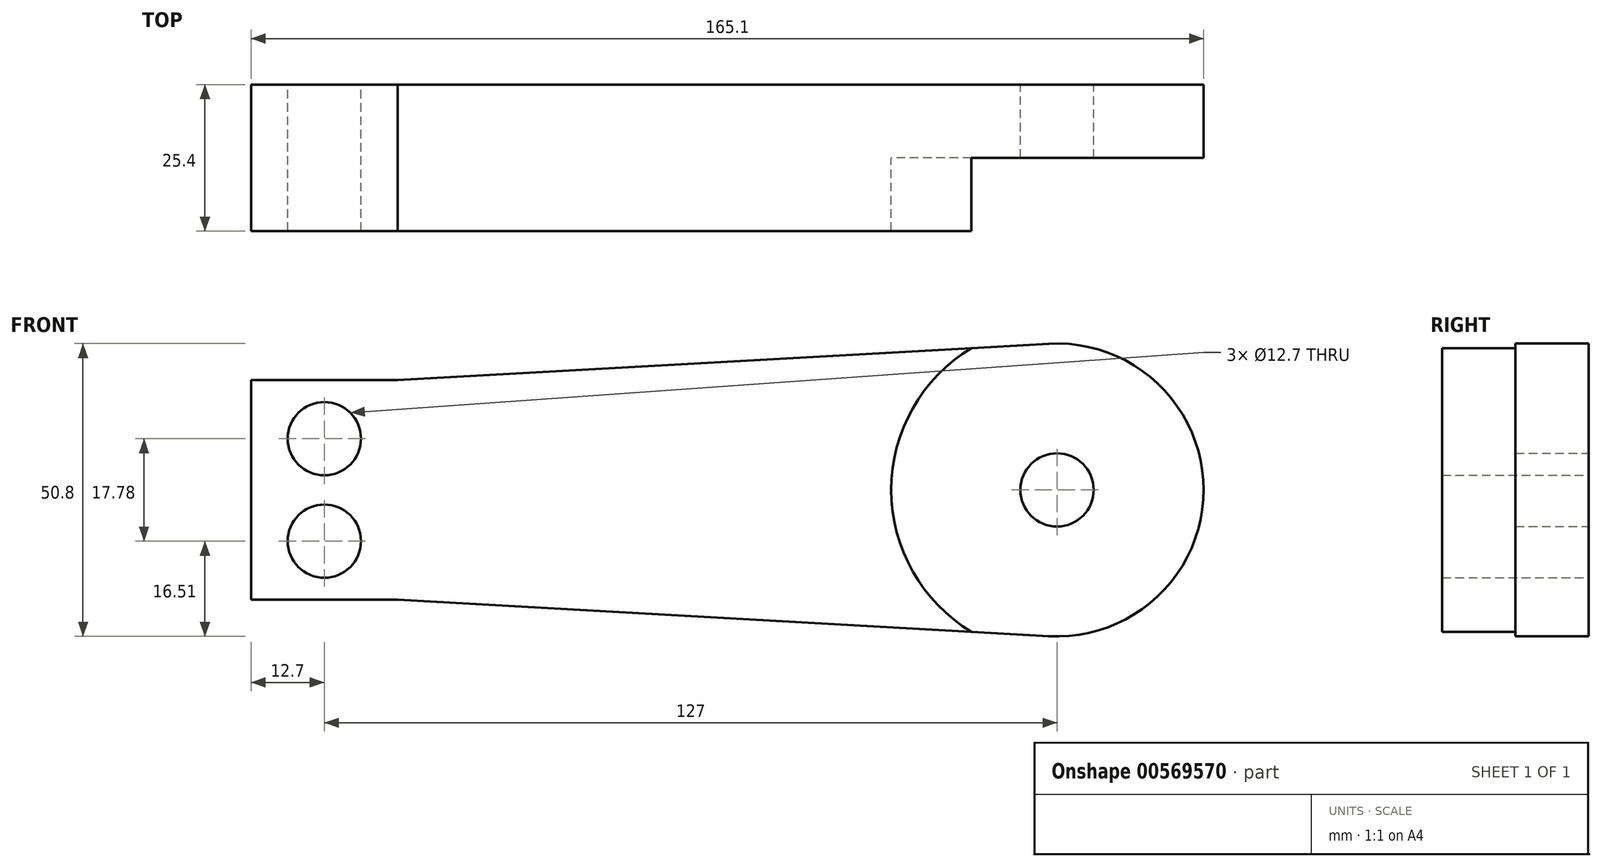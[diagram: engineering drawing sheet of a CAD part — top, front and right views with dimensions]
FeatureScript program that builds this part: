
annotation { "Feature Type Name" : "Feature", "Feature Type Description" : "" }
export const myFeature = defineFeature(function(context is Context, id is Id, definition is map)
    precondition{}
    {
        {
            var Q0;
            Q0=qCreatedBy(makeId("Front.planeOp"),FACE);
            var sketch = newSketch(context, id + "F0", { "sketchPlane" : qUnion([Q0])});
            skCircle(sketch, "E0", {"center": v(0, 0) * mm, "radius": 25.4 * mm});
            skLineSegment(sketch, "E1.bottom", {"start": v(-139.7, 19.05) * mm, "end": v(-114.3, 19.05) * mm});
            skLineSegment(sketch, "E1.top", {"start": v(-139.7, -19.05) * mm, "end": v(-114.3, -19.05) * mm});
            skLineSegment(sketch, "E1.left", {"start": v(-139.7, 19.05) * mm, "end": v(-139.7, -19.05) * mm});
            skLineSegment(sketch, "E1.right", {"start": v(-114.3, 19.05) * mm, "end": v(-114.3, -19.05) * mm});
            skPoint(sketch, "E1.middle", {"position": v(-127, 0) * mm});
            skLineSegment(sketch, "E2", {"start": v(-114.3, 19.05) * mm, "end": v(-1.42, 25.36) * mm});
            skLineSegment(sketch, "E3", {"start": v(-114.3, -19.05) * mm, "end": v(-1.42, -25.36) * mm});
            skCircle(sketch, "E4", {"center": v(0, 0) * mm, "radius": 6.35 * mm});
            skCircle(sketch, "E5", {"center": v(-127, 8.89) * mm, "radius": 6.35 * mm});
            skCircle(sketch, "E6", {"center": v(-127, -8.9) * mm, "radius": 6.35 * mm});
            skArc(sketch, "E7", {"start": v(-14.83, -24.61) * mm, "mid": v(-28.73, 0) * mm, "end": v(-14.83, 24.61) * mm});
            skSolve(sketch);
        }
        {
            var Q0;
            Q0 = qSketchRegion(id + "F0", true);
            extrude(context, id + "F1", {"entities" : qUnion([Q0]), "depth" : 12.7 * mm, "offsetDistance" : 25.4 * mm});
        }
        {
            var Q0;
            {var subQ0=sQuery(id+"F0.wireOp",EDGE,"E1.right");Q0=makeQuery(id+"F0.imprint","IMPRINT",FACE,{"disambiguationData":[TD([[makeQuery(id+"F0.imprint","IMPRINT",EDGE,{"derivedFrom":subQ0}),1.0]])]});}
            var Q1;
            Q1=makeQuery(id+"F0.imprint","IMPRINT",FACE,{"disambiguationData":[TD([[makeQuery(id+"F0.imprint","IMPRINT",EDGE,{"derivedFrom":sQuery(id+"F0.wireOp",EDGE,"E1.bottom")}),-1.0]])]});
            extrude(context, id + "F2", {"entities" : qUnion([Q0, Q1]), "operationType" : NewBodyOperationType.ADD, "depth" : 25.4 * mm, "offsetDistance" : 25.4 * mm});
        }
    });
